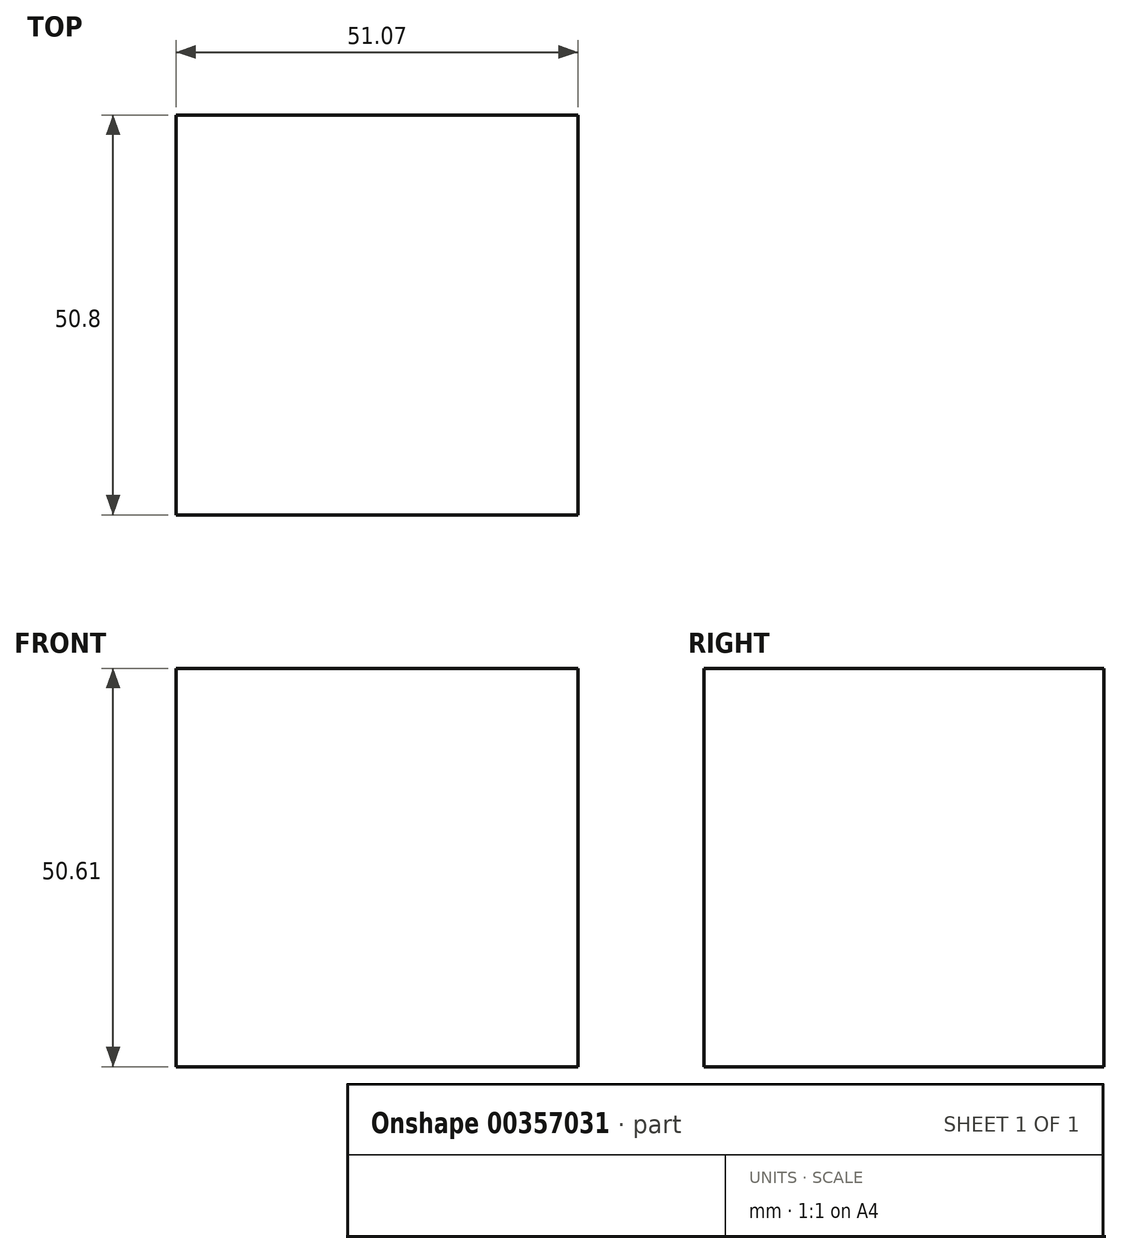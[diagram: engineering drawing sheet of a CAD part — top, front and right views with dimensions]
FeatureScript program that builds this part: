
annotation { "Feature Type Name" : "Feature", "Feature Type Description" : "" }
export const myFeature = defineFeature(function(context is Context, id is Id, definition is map)
    precondition{}
    {
        {
            var Q0;
            Q0=qCreatedBy(makeId("Front.planeOp"),FACE);
            var sketch = newSketch(context, id + "F0", { "sketchPlane" : qUnion([Q0])});
            skLineSegment(sketch, "E0", {"start": v(0, 0) * mm, "end": v(51.07, 0) * mm});
            skLineSegment(sketch, "E1", {"start": v(51.07, 0) * mm, "end": v(51.07, 50.6) * mm});
            skLineSegment(sketch, "E2", {"start": v(51.07, 50.6) * mm, "end": v(0, 50.6) * mm});
            skLineSegment(sketch, "E3", {"start": v(0, 50.6) * mm, "end": v(0, 0) * mm});
            skSolve(sketch);
        }
        {
            var Q0;
            Q0 = qSketchRegion(id + "F0", true);
            extrude(context, id + "F1", {"entities" : qUnion([Q0]), "depth" : 50.8 * mm});
        }
    });
